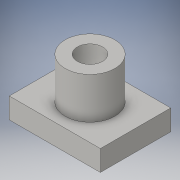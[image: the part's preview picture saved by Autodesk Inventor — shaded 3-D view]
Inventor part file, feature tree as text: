
AUTODESK INVENTOR PART (.ipt)
format: ipt  version: 2016 (Build 200138000, 138)  size: 233,472 bytes
history: native  units: in
note: dims shown in document units (in); Inventor stores cm internally (conversion verified against a paired STEP export)
features: extrude x2, sketch x2
ambient origin geometry x8: Origin, YZ Plane, XZ Plane, XY Plane, X Axis, Y Axis, Z Axis, Center Point
bodies: Solid1 (feature_tree)
feature tree (4):
  extrude  "Extrusion1"  Depth=0.6693in
  extrude  "Extrusion2"  Depth=0.3937in
  sketch  "Sketch1"  dims[d0=0.8661in d1=0.6693in]
  sketch  "Sketch2"  dims[d2=0.1969in d3=0.0in d4=0.4724in d5=0.2402in d6=0.3937in d7=0.0in]
